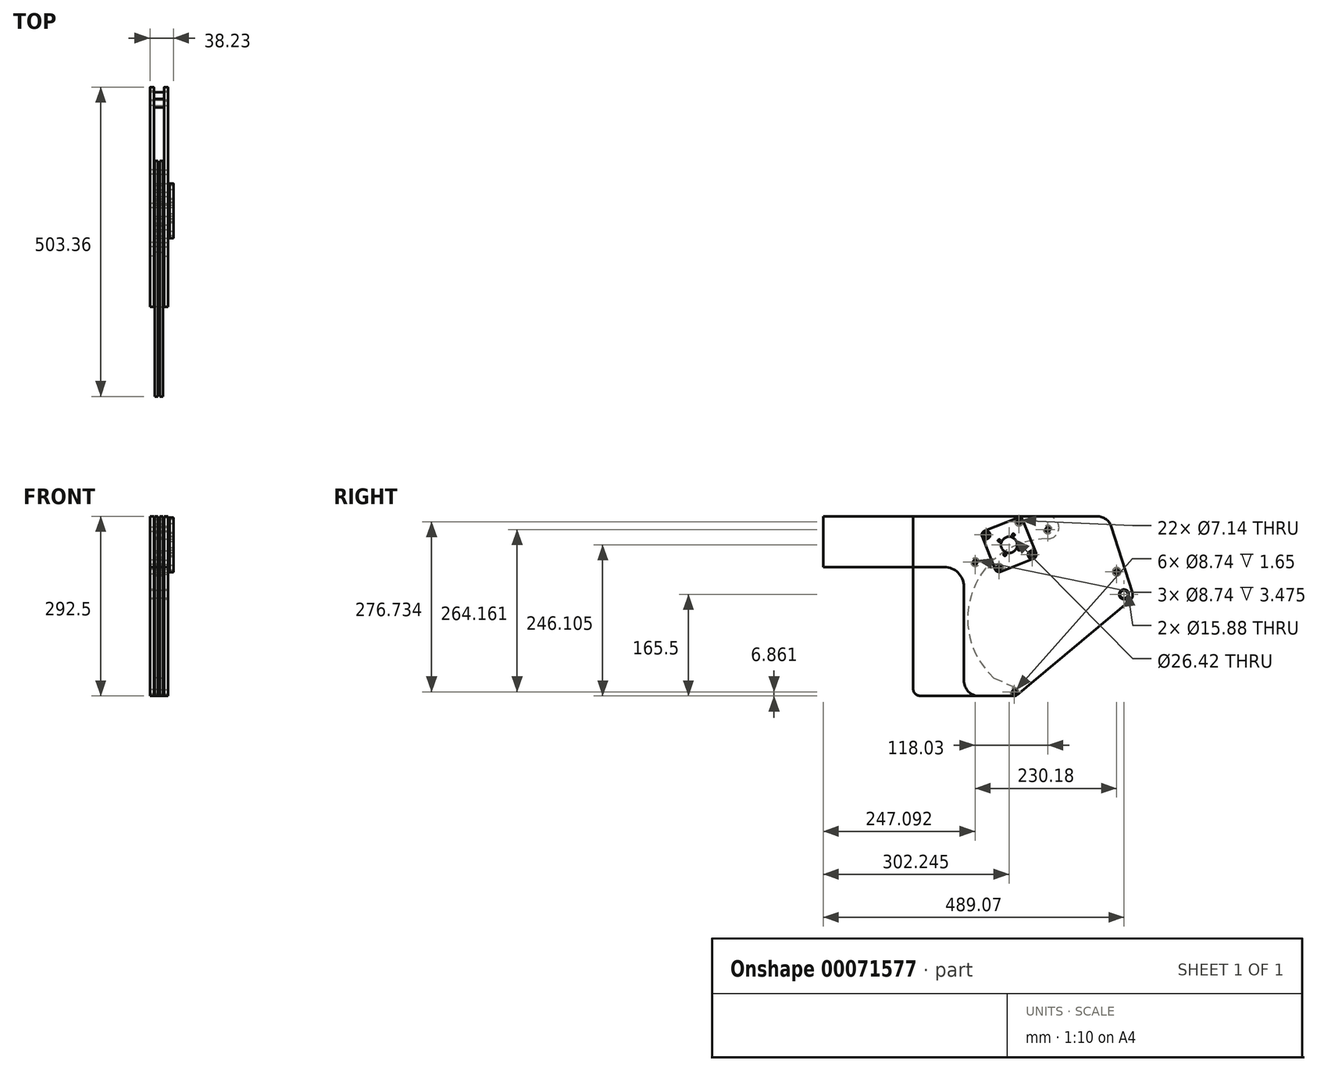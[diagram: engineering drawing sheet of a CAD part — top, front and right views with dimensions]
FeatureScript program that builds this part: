
annotation { "Feature Type Name" : "Feature", "Feature Type Description" : "" }
export const myFeature = defineFeature(function(context is Context, id is Id, definition is map)
    precondition{}
    {
        {
            assignVariable(context, id + "F0", {"name" : "overallWidth", "anyValue" : 29});
        }
        {
            assignVariable(context, id + "F1", {"name" : "bumperGapWidth", "anyValue" : 13});
        }
        {
            var Q0;
            Q0=qCreatedBy(makeId("Right.planeOp"),FACE);
            var sketch = newSketch(context, id + "F2", { "sketchPlane" : qUnion([Q0])});
            skLineSegment(sketch, "E0", {"start": v(0, 0) * mm, "end": v(-374.65, 0) * mm, "construction": true});
            skLineSegment(sketch, "E1", {"start": v(0, 0) * mm, "end": v(0, 234.95) * mm, "construction": true});
            skCircle(sketch, "E2", {"center": v(0, 234.95) * mm, "radius": 6.35 * mm});
            skCircle(sketch, "E3", {"center": v(-178.27, 76.31) * mm, "radius": 3.57 * mm});
            skCircle(sketch, "E4", {"center": v(-67.8, 123.83) * mm, "radius": 123.83 * mm, "construction": true});
            skLineSegment(sketch, "E5.bottom", {"start": v(-343.02, 279.4) * mm, "end": v(-323.97, 279.4) * mm, "construction": true});
            skLineSegment(sketch, "E5.top", {"start": v(-343.02, 152.4) * mm, "end": v(-323.97, 152.4) * mm, "construction": true});
            skLineSegment(sketch, "E5.left", {"start": v(-343.02, 279.4) * mm, "end": v(-343.02, 152.4) * mm, "construction": true});
            skLineSegment(sketch, "E5.right", {"start": v(-323.97, 279.4) * mm, "end": v(-323.97, 152.4) * mm, "construction": true});
            skCircle(sketch, "E6", {"center": v(-292.22, 184.15) * mm, "radius": 31.75 * mm, "construction": true});
            skCircle(sketch, "E7", {"center": v(-292.22, 247.65) * mm, "radius": 31.75 * mm, "construction": true});
            skLineSegment(sketch, "E8", {"start": v(-323.97, 279.4) * mm, "end": v(-292.22, 279.4) * mm, "construction": true});
            skLineSegment(sketch, "E9", {"start": v(-260.47, 247.65) * mm, "end": v(-260.47, 184.15) * mm, "construction": true});
            skLineSegment(sketch, "E10", {"start": v(-323.97, 152.4) * mm, "end": v(-292.22, 152.4) * mm, "construction": true});
            skCircle(sketch, "E11", {"center": v(-123.95, 195.17) * mm, "radius": 123.83 * mm, "construction": true});
            skLineSegment(sketch, "E12", {"start": v(-343.02, 361.95) * mm, "end": v(6.35, 361.95) * mm, "construction": true});
            skLineSegment(sketch, "E13", {"start": v(6.35, 361.95) * mm, "end": v(6.35, 234.95) * mm, "construction": true});
            skCircle(sketch, "E14", {"center": v(-11.8, 271.71) * mm, "radius": 3.57 * mm});
            skCircle(sketch, "E15", {"center": v(-241.98, 287.3) * mm, "radius": 3.57 * mm});
            skCircle(sketch, "E16", {"center": v(-123.95, 340.47) * mm, "radius": 3.57 * mm});
            skLineSegment(sketch, "E17", {"start": v(0, 234.95) * mm, "end": v(-11.8, 271.71) * mm, "construction": true});
            skLineSegment(sketch, "E18", {"start": v(-6.05, 233) * mm, "end": v(-17.84, 269.77) * mm, "construction": true});
            skLineSegment(sketch, "E19", {"start": v(-123.95, 319) * mm, "end": v(-123.95, 361.95) * mm, "construction": true});
            skCircle(sketch, "E20", {"center": v(-178.27, 76.31) * mm, "radius": 4.37 * mm});
            skCircle(sketch, "E21", {"center": v(-178.27, 76.31) * mm, "radius": 6.86 * mm});
            skCircle(sketch, "E22", {"center": v(-241.98, 287.3) * mm, "radius": 4.37 * mm});
            skCircle(sketch, "E23", {"center": v(-241.98, 287.3) * mm, "radius": 6.86 * mm});
            skCircle(sketch, "E24", {"center": v(-123.95, 340.47) * mm, "radius": 4.37 * mm});
            skCircle(sketch, "E25", {"center": v(-123.95, 340.47) * mm, "radius": 6.86 * mm});
            skCircle(sketch, "E26", {"center": v(-11.8, 271.71) * mm, "radius": 4.37 * mm});
            skCircle(sketch, "E27", {"center": v(-11.8, 271.71) * mm, "radius": 6.86 * mm});
            skSolve(sketch);
        }
        {
            var Q0;
            Q0=qCreatedBy(makeId("Right.planeOp"),FACE);
            cPlane(context, id + "F3", {"entities" : qUnion([Q0]), "cplaneType" : CPlaneType.OFFSET, "offset" : (getVariable(context, 'bumperGapWidth') / 2) * mm, "width" : 152.4 * mm, "height" : 152.4 * mm});
        }
        {
            var Q0;
            Q0=qCreatedBy(makeId("Right.planeOp"),FACE);
            cPlane(context, id + "F4", {"entities" : qUnion([Q0]), "cplaneType" : CPlaneType.OFFSET, "offset" : (getVariable(context, 'overallWidth') / 2) * mm, "width" : 152.4 * mm, "height" : 152.4 * mm});
        }
        {
            var Q0;
            Q0=qCreatedBy(id+"F4.planeOp",FACE);
            var sketch = newSketch(context, id + "F5", { "sketchPlane" : qUnion([Q0])});
            skCircle(sketch, "E28.0", {"center": v(-178.27, 76.31) * mm, "radius": 6.86 * mm});
            skCircle(sketch, "E28.1", {"center": v(-178.27, 76.31) * mm, "radius": 3.57 * mm});
            skCircle(sketch, "E28.7", {"center": v(-241.98, 287.3) * mm, "radius": 3.57 * mm});
            skCircle(sketch, "E28.8", {"center": v(-123.95, 340.47) * mm, "radius": 3.57 * mm});
            skCircle(sketch, "E28.9", {"center": v(-11.8, 271.71) * mm, "radius": 3.57 * mm});
            skLineSegment(sketch, "E29.0", {"start": v(-343.02, 279.4) * mm, "end": v(-323.97, 279.4) * mm, "construction": true});
            skLineSegment(sketch, "E29.1", {"start": v(-323.97, 279.4) * mm, "end": v(-292.22, 279.4) * mm, "construction": true});
            skCircle(sketch, "E29.2", {"center": v(-292.22, 247.65) * mm, "radius": 31.75 * mm, "construction": true});
            skLineSegment(sketch, "E30", {"start": v(-260.47, 247.65) * mm, "end": v(-260.47, 94.85) * mm});
            skLineSegment(sketch, "E31", {"start": v(-235.07, 69.45) * mm, "end": v(-178.27, 69.45) * mm});
            skArc(sketch, "E32", {"start": v(-260.47, 247.65) * mm, "mid": v(-269.77, 270.1) * mm, "end": v(-292.22, 279.4) * mm});
            skPoint(sketch, "E33.visualSharp", {"position": v(-260.47, 69.45) * mm});
            skArc(sketch, "E33.filletArc", {"start": v(-260.47, 94.85) * mm, "mid": v(-253.03, 76.9) * mm, "end": v(-235.07, 69.45) * mm});
            skCircle(sketch, "E34", {"center": v(0, 234.95) * mm, "radius": 7.94 * mm});
            skCircle(sketch, "E35", {"center": v(0, 234.95) * mm, "radius": 14.29 * mm, "construction": true});
            skLineSegment(sketch, "E36", {"start": v(-173.87, 71.05) * mm, "end": v(9.16, 223.99) * mm});
            skLineSegment(sketch, "E37", {"start": v(13.6, 239.32) * mm, "end": v(-20.1, 344.31) * mm});
            skLineSegment(sketch, "E38.0", {"start": v(-343.02, 361.95) * mm, "end": v(6.35, 361.95) * mm, "construction": true});
            skLineSegment(sketch, "E39", {"start": v(-44.28, 361.95) * mm, "end": v(-343.02, 361.95) * mm});
            skLineSegment(sketch, "E40", {"start": v(-343.02, 361.95) * mm, "end": v(-343.02, 279.4) * mm});
            skArc(sketch, "E41", {"start": v(-178.27, 69.45) * mm, "mid": v(-175.93, 69.86) * mm, "end": v(-173.87, 71.05) * mm});
            skArc(sketch, "E42", {"start": v(9.16, 223.99) * mm, "mid": v(13.72, 230.97) * mm, "end": v(13.6, 239.32) * mm});
            skLineSegment(sketch, "E43", {"start": v(-343.02, 279.4) * mm, "end": v(-292.22, 279.4) * mm, "construction": true});
            skLineSegment(sketch, "E44", {"start": v(-343.02, 279.4) * mm, "end": v(-292.22, 279.4) * mm});
            skPoint(sketch, "E45.visualSharp", {"position": v(-25.75, 361.95) * mm});
            skArc(sketch, "E45.filletArc", {"start": v(-20.1, 344.31) * mm, "mid": v(-29.31, 357.07) * mm, "end": v(-44.28, 361.95) * mm});
            skSolve(sketch);
        }
        {
            var Q0;
            Q0 = qSketchRegion(id + "F5", true);
            extrude(context, id + "F6", {"entities" : qUnion([Q0]), "oppositeDirection" : true, "depth" : 6.35 * mm});
        }
        {
            var Q0;
            Q0=qCreatedBy(id+"F3.planeOp",FACE);
            var sketch = newSketch(context, id + "F7", { "sketchPlane" : qUnion([Q0])});
            skCircle(sketch, "E46.0", {"center": v(-123.95, 195.17) * mm, "radius": 123.83 * mm, "construction": true});
            skCircle(sketch, "E47", {"center": v(-123.95, 195.17) * mm, "radius": 130.18 * mm, "construction": true});
            skLineSegment(sketch, "E48.0", {"start": v(-343.02, 279.4) * mm, "end": v(-323.97, 279.4) * mm, "construction": true});
            skLineSegment(sketch, "E49.0", {"start": v(-323.97, 279.4) * mm, "end": v(-323.97, 152.4) * mm, "construction": true});
            skLineSegment(sketch, "E50", {"start": v(-362.07, 361.95) * mm, "end": v(-362.07, 279.4) * mm, "construction": true});
            skLineSegment(sketch, "E51", {"start": v(-362.07, 279.4) * mm, "end": v(-343.02, 279.4) * mm});
            skLineSegment(sketch, "E52", {"start": v(-343.02, 279.4) * mm, "end": v(-343.02, 152.4) * mm});
            skCircle(sketch, "E53.0", {"center": v(-178.27, 76.31) * mm, "radius": 3.57 * mm, "construction": true});
            skLineSegment(sketch, "E54", {"start": v(-343.02, 82.15) * mm, "end": v(-343.02, 152.4) * mm});
            skArc(sketch, "E55", {"start": v(-211.94, 99.24) * mm, "mid": v(-245.26, 242.38) * mm, "end": v(-123.95, 325.34) * mm});
            skLineSegment(sketch, "E56", {"start": v(-211.94, 99.24) * mm, "end": v(-175.42, 82.55) * mm});
            skCircle(sketch, "E57.0", {"center": v(-178.27, 76.31) * mm, "radius": 6.86 * mm, "construction": true});
            skArc(sketch, "E58", {"start": v(-178.27, 69.45) * mm, "mid": v(-171.57, 74.85) * mm, "end": v(-175.42, 82.55) * mm, "construction": true});
            skLineSegment(sketch, "E59", {"start": v(-178.27, 69.45) * mm, "end": v(-330.32, 69.45) * mm});
            skCircle(sketch, "E60.0", {"center": v(-241.98, 287.3) * mm, "radius": 3.57 * mm});
            skCircle(sketch, "E61.0", {"center": v(-123.95, 340.47) * mm, "radius": 3.57 * mm});
            skArc(sketch, "E62", {"start": v(-178.27, 69.45) * mm, "mid": v(-171.57, 74.85) * mm, "end": v(-175.42, 82.55) * mm});
            skCircle(sketch, "E63.0", {"center": v(-178.27, 76.31) * mm, "radius": 3.57 * mm});
            skPoint(sketch, "E64.visualSharp", {"position": v(-343.02, 69.45) * mm});
            skArc(sketch, "E64.filletArc", {"start": v(-343.02, 82.15) * mm, "mid": v(-339.3, 73.17) * mm, "end": v(-330.32, 69.45) * mm});
            skArc(sketch, "E65", {"start": v(-123.95, 325.34) * mm, "mid": v(-105.65, 343.65) * mm, "end": v(-123.95, 361.95) * mm});
            skLineSegment(sketch, "E66", {"start": v(-123.95, 361.95) * mm, "end": v(-362.07, 361.95) * mm});
            skLineSegment(sketch, "E67", {"start": v(-362.07, 361.95) * mm, "end": v(-489.07, 361.95) * mm});
            skLineSegment(sketch, "E68", {"start": v(-489.07, 361.95) * mm, "end": v(-489.07, 279.4) * mm});
            skLineSegment(sketch, "E69", {"start": v(-489.07, 279.4) * mm, "end": v(-362.07, 279.4) * mm});
            skSolve(sketch);
        }
        {
            var Q0;
            Q0 = qSketchRegion(id + "F7", true);
            extrude(context, id + "F8", {"entities" : qUnion([Q0]), "oppositeDirection" : true, "depth" : 4.76 * mm});
        }
        {
            var Q0;
            Q0=makeQuery(id+"F8.opExtrude","CAP_FACE",FACE,{"disambiguationData":[OSD([sQuery(id+"F7.wireOp",EDGE,"FGU2iulP-mEND-ptDn-2N6M-zOusOUoRXGuS"),sQuery(id+"F7.wireOp",EDGE,"dHuU5Xxs-PWdM-lHFD-YR0q-5kX4qnVROPGa"),sQuery(id+"F7.wireOp",EDGE,"emKYSds7-kRQy-B5Ny-Edj4-jaAremwDHOBO"),sQuery(id+"F7.wireOp",EDGE,"E50"),sQuery(id+"F7.wireOp",EDGE,"E51"),sQuery(id+"F7.wireOp",EDGE,"E52"),sQuery(id+"F7.wireOp",EDGE,"E54"),sQuery(id+"F7.wireOp",EDGE,"E55"),sQuery(id+"F7.wireOp",EDGE,"a4eece87-18dd-42ed-a909-83406d0543b2"),sQuery(id+"F7.wireOp",EDGE,"E56"),sQuery(id+"F7.wireOp",EDGE,"E59"),sQuery(id+"F7.wireOp",EDGE,"E60.0"),sQuery(id+"F7.wireOp",EDGE,"E61.0"),sQuery(id+"F7.wireOp",EDGE,"e2687a6c-33c6-4455-bcdd-d88ace95f83b.0"),sQuery(id+"F7.wireOp",EDGE,"E62"),sQuery(id+"F7.wireOp",EDGE,"E63.0"),sQuery(id+"F7.wireOp",EDGE,"eee57473-292c-4d81-84d7-392532a5bbb9.filletArc"),sQuery(id+"F7.wireOp",EDGE,"E64.filletArc")])],"isStart":true});
            var sketch = newSketch(context, id + "F9", { "sketchPlane" : qUnion([Q0])});
            skCircle(sketch, "E70.0", {"center": v(-241.98, 287.3) * mm, "radius": 6.86 * mm});
            skCircle(sketch, "E70.1", {"center": v(-241.98, 287.3) * mm, "radius": 4.37 * mm});
            skCircle(sketch, "E70.2", {"center": v(-123.95, 340.47) * mm, "radius": 6.86 * mm});
            skCircle(sketch, "E70.3", {"center": v(-123.95, 340.47) * mm, "radius": 4.37 * mm});
            skCircle(sketch, "E70.4", {"center": v(-11.8, 271.71) * mm, "radius": 6.86 * mm});
            skCircle(sketch, "E70.5", {"center": v(-11.8, 271.71) * mm, "radius": 4.37 * mm});
            skCircle(sketch, "E70.6", {"center": v(-178.27, 76.31) * mm, "radius": 6.86 * mm});
            skCircle(sketch, "E70.7", {"center": v(-178.27, 76.31) * mm, "radius": 4.37 * mm});
            skSolve(sketch);
        }
        {
            var Q0;
            Q0=makeQuery(id+"F9.imprint","IMPRINT",FACE,{"disambiguationData":[TD([[makeQuery(id+"F9.imprint","IMPRINT",EDGE,{"derivedFrom":sQuery(id+"F9.wireOp",EDGE,"E70.2")}),1.0]])]});
            var Q1;
            Q1=makeQuery(id+"F9.imprint","IMPRINT",FACE,{"disambiguationData":[TD([[makeQuery(id+"F9.imprint","IMPRINT",EDGE,{"derivedFrom":sQuery(id+"F9.wireOp",EDGE,"E70.0")}),1.0]])]});
            var Q2;
            Q2=makeQuery(id+"F9.imprint","IMPRINT",FACE,{"disambiguationData":[TD([[makeQuery(id+"F9.imprint","IMPRINT",EDGE,{"derivedFrom":sQuery(id+"F9.wireOp",EDGE,"E70.7")}),-1.0]])]});
            var Q3;
            Q3=makeQuery(id+"F6.opExtrude","CAP_FACE",FACE,{"disambiguationData":[OSD([sQuery(id+"F5.wireOp",EDGE,"E28.0"),sQuery(id+"F5.wireOp",EDGE,"E28.1"),sQuery(id+"F5.wireOp",EDGE,"E28.2"),sQuery(id+"F5.wireOp",EDGE,"E28.3"),sQuery(id+"F5.wireOp",EDGE,"E28.4"),sQuery(id+"F5.wireOp",EDGE,"E28.5"),sQuery(id+"F5.wireOp",EDGE,"E28.6"),sQuery(id+"F5.wireOp",EDGE,"E28.7"),sQuery(id+"F5.wireOp",EDGE,"E28.8"),sQuery(id+"F5.wireOp",EDGE,"E28.9"),sQuery(id+"F5.wireOp",EDGE,"0DRxkcYK-P67Z-hc5T-PIY5-J2nq71u3PR2t"),sQuery(id+"F5.wireOp",EDGE,"E30"),sQuery(id+"F5.wireOp",EDGE,"E31"),sQuery(id+"F5.wireOp",EDGE,"xV87OUrw-cdUr-jH3c-AOfr-qMSfTrLvHBVd"),sQuery(id+"F5.wireOp",EDGE,"E32"),sQuery(id+"F5.wireOp",EDGE,"E33.filletArc")])],"isStart":false});
            extrude(context, id + "F10", {"entities" : qUnion([Q0, Q1, Q2]), "endBound" : BoundingType.UP_TO_SURFACE, "endBoundEntityFace" : qUnion([Q3]), "depth" : 25.4 * mm});
        }
        {
            var Q0;
            Q0=makeQuery(id+"F8.opExtrude","SWEPT_BODY",BODY,{"disambiguationData":[OSD([sQuery(id+"F7.wireOp",EDGE,"FGU2iulP-mEND-ptDn-2N6M-zOusOUoRXGuS"),sQuery(id+"F7.wireOp",EDGE,"dHuU5Xxs-PWdM-lHFD-YR0q-5kX4qnVROPGa"),sQuery(id+"F7.wireOp",EDGE,"emKYSds7-kRQy-B5Ny-Edj4-jaAremwDHOBO"),sQuery(id+"F7.wireOp",EDGE,"E50"),sQuery(id+"F7.wireOp",EDGE,"E51"),sQuery(id+"F7.wireOp",EDGE,"E52"),sQuery(id+"F7.wireOp",EDGE,"E54"),sQuery(id+"F7.wireOp",EDGE,"E55"),sQuery(id+"F7.wireOp",EDGE,"a4eece87-18dd-42ed-a909-83406d0543b2"),sQuery(id+"F7.wireOp",EDGE,"E56"),sQuery(id+"F7.wireOp",EDGE,"E59"),sQuery(id+"F7.wireOp",EDGE,"E60.0"),sQuery(id+"F7.wireOp",EDGE,"E61.0"),sQuery(id+"F7.wireOp",EDGE,"e2687a6c-33c6-4455-bcdd-d88ace95f83b.0"),sQuery(id+"F7.wireOp",EDGE,"E62"),sQuery(id+"F7.wireOp",EDGE,"E63.0"),sQuery(id+"F7.wireOp",EDGE,"eee57473-292c-4d81-84d7-392532a5bbb9.filletArc"),sQuery(id+"F7.wireOp",EDGE,"E64.filletArc")])]});
            var Q1;
            Q1=makeQuery(id+"F6.opExtrude","SWEPT_BODY",BODY,{"disambiguationData":[OSD([sQuery(id+"F5.wireOp",EDGE,"E28.0"),sQuery(id+"F5.wireOp",EDGE,"E28.1"),sQuery(id+"F5.wireOp",EDGE,"E28.2"),sQuery(id+"F5.wireOp",EDGE,"E28.3"),sQuery(id+"F5.wireOp",EDGE,"E28.4"),sQuery(id+"F5.wireOp",EDGE,"E28.5"),sQuery(id+"F5.wireOp",EDGE,"E28.6"),sQuery(id+"F5.wireOp",EDGE,"E28.7"),sQuery(id+"F5.wireOp",EDGE,"E28.8"),sQuery(id+"F5.wireOp",EDGE,"E28.9"),sQuery(id+"F5.wireOp",EDGE,"0DRxkcYK-P67Z-hc5T-PIY5-J2nq71u3PR2t"),sQuery(id+"F5.wireOp",EDGE,"E30"),sQuery(id+"F5.wireOp",EDGE,"E31"),sQuery(id+"F5.wireOp",EDGE,"xV87OUrw-cdUr-jH3c-AOfr-qMSfTrLvHBVd"),sQuery(id+"F5.wireOp",EDGE,"E32"),sQuery(id+"F5.wireOp",EDGE,"E33.filletArc")])]});
            var Q2;
            Q2=makeQuery(id+"F10.opExtrude","SWEPT_BODY",BODY,{"disambiguationData":[OSD([sQuery(id+"F9.wireOp",EDGE,"E70.2"),sQuery(id+"F9.wireOp",EDGE,"E70.3")])]});
            var Q3;
            Q3=makeQuery(id+"F10.opExtrude","SWEPT_BODY",BODY,{"disambiguationData":[OSD([sQuery(id+"F9.wireOp",EDGE,"E70.4"),sQuery(id+"F9.wireOp",EDGE,"E70.5")])]});
            var Q4;
            Q4=makeQuery(id+"F10.opExtrude","SWEPT_BODY",BODY,{"disambiguationData":[OSD([sQuery(id+"F9.wireOp",EDGE,"E70.6"),sQuery(id+"F9.wireOp",EDGE,"E70.7")])]});
            var Q5;
            Q5=makeQuery(id+"F10.opExtrude","SWEPT_BODY",BODY,{"disambiguationData":[OSD([sQuery(id+"F9.wireOp",EDGE,"E70.0"),sQuery(id+"F9.wireOp",EDGE,"E70.1")])]});
            var Q6;
            Q6=qCreatedBy(makeId("Right.planeOp"),FACE);
            mirror(context, id + "F11", {"entities" : qUnion([Q0, Q1, Q2, Q3, Q4, Q5]), "mirrorPlane" : qUnion([Q6])});
        }
        {
            var Q0;
            Q0=makeQuery(id+"F9.imprint","IMPRINT",FACE,{"disambiguationData":[TD([[makeQuery(id+"F9.imprint","IMPRINT",EDGE,{"derivedFrom":sQuery(id+"F9.wireOp",EDGE,"E70.4")}),1.0]])]});
            extrude(context, id + "F12", {"entities" : qUnion([Q0]), "endBound" : BoundingType.UP_TO_NEXT, "depth" : 25.4 * mm, "hasSecondDirection" : true, "secondDirectionBound" : SecondDirectionBoundingType.UP_TO_NEXT, "secondDirectionOppositeDirection" : true, "secondDirectionDepth" : 25.4 * mm});
        }
        {
            var Q0;
            Q0=makeQuery(id+"F11.opPattern","COPY",FACE,{"derivedFrom":makeQuery(id+"F8.opExtrude","CAP_FACE",FACE,{"disambiguationData":[OSD([sQuery(id+"F7.wireOp",EDGE,"FGU2iulP-mEND-ptDn-2N6M-zOusOUoRXGuS"),sQuery(id+"F7.wireOp",EDGE,"dHuU5Xxs-PWdM-lHFD-YR0q-5kX4qnVROPGa"),sQuery(id+"F7.wireOp",EDGE,"emKYSds7-kRQy-B5Ny-Edj4-jaAremwDHOBO"),sQuery(id+"F7.wireOp",EDGE,"E50"),sQuery(id+"F7.wireOp",EDGE,"E51"),sQuery(id+"F7.wireOp",EDGE,"E52"),sQuery(id+"F7.wireOp",EDGE,"E54"),sQuery(id+"F7.wireOp",EDGE,"E55"),sQuery(id+"F7.wireOp",EDGE,"a4eece87-18dd-42ed-a909-83406d0543b2"),sQuery(id+"F7.wireOp",EDGE,"E56"),sQuery(id+"F7.wireOp",EDGE,"E59"),sQuery(id+"F7.wireOp",EDGE,"E60.0"),sQuery(id+"F7.wireOp",EDGE,"E61.0"),sQuery(id+"F7.wireOp",EDGE,"e2687a6c-33c6-4455-bcdd-d88ace95f83b.0"),sQuery(id+"F7.wireOp",EDGE,"E62"),sQuery(id+"F7.wireOp",EDGE,"E63.0"),sQuery(id+"F7.wireOp",EDGE,"eee57473-292c-4d81-84d7-392532a5bbb9.filletArc"),sQuery(id+"F7.wireOp",EDGE,"E64.filletArc")])],"isStart":false}),"instanceName":"1"});
            var sketch = newSketch(context, id + "F13", { "sketchPlane" : qUnion([Q0])});
            skCircle(sketch, "E71.0", {"center": v(-241.98, 287.3) * mm, "radius": 4.37 * mm});
            skCircle(sketch, "E71.1", {"center": v(-241.98, 287.3) * mm, "radius": 6.86 * mm});
            skCircle(sketch, "E71.2", {"center": v(-123.95, 340.47) * mm, "radius": 6.86 * mm});
            skCircle(sketch, "E71.3", {"center": v(-123.95, 340.47) * mm, "radius": 4.37 * mm});
            skCircle(sketch, "E71.6", {"center": v(-178.27, 76.31) * mm, "radius": 6.86 * mm});
            skCircle(sketch, "E71.7", {"center": v(-178.27, 76.31) * mm, "radius": 4.37 * mm});
            skSolve(sketch);
        }
        {
            var Q0;
            Q0 = qSketchRegion(id + "F13", true);
            var Q1;
            Q1=makeQuery(id+"F8.opExtrude","CAP_FACE",FACE,{"disambiguationData":[OSD([sQuery(id+"F7.wireOp",EDGE,"FGU2iulP-mEND-ptDn-2N6M-zOusOUoRXGuS"),sQuery(id+"F7.wireOp",EDGE,"dHuU5Xxs-PWdM-lHFD-YR0q-5kX4qnVROPGa"),sQuery(id+"F7.wireOp",EDGE,"emKYSds7-kRQy-B5Ny-Edj4-jaAremwDHOBO"),sQuery(id+"F7.wireOp",EDGE,"E50"),sQuery(id+"F7.wireOp",EDGE,"E51"),sQuery(id+"F7.wireOp",EDGE,"E52"),sQuery(id+"F7.wireOp",EDGE,"E54"),sQuery(id+"F7.wireOp",EDGE,"E55"),sQuery(id+"F7.wireOp",EDGE,"a4eece87-18dd-42ed-a909-83406d0543b2"),sQuery(id+"F7.wireOp",EDGE,"E56"),sQuery(id+"F7.wireOp",EDGE,"E59"),sQuery(id+"F7.wireOp",EDGE,"E60.0"),sQuery(id+"F7.wireOp",EDGE,"E61.0"),sQuery(id+"F7.wireOp",EDGE,"e2687a6c-33c6-4455-bcdd-d88ace95f83b.0"),sQuery(id+"F7.wireOp",EDGE,"E62"),sQuery(id+"F7.wireOp",EDGE,"E63.0"),sQuery(id+"F7.wireOp",EDGE,"eee57473-292c-4d81-84d7-392532a5bbb9.filletArc"),sQuery(id+"F7.wireOp",EDGE,"E64.filletArc")])],"isStart":false});
            extrude(context, id + "F14", {"entities" : qUnion([Q0]), "endBound" : BoundingType.UP_TO_SURFACE, "endBoundEntityFace" : qUnion([Q1]), "depth" : 25.4 * mm});
        }
        {
            var Q0;
            Q0=makeQuery(id+"F2.imprint","IMPRINT",FACE,{"disambiguationData":[TD([[makeQuery(id+"F2.imprint","IMPRINT",EDGE,{"derivedFrom":sQuery(id+"F2.wireOp",EDGE,"E2")}),1.0]])]});
            var Q1;
            Q1=sQuery(id+"F2.wireOp",EDGE,"E2");
            extrude(context, id + "F15", {"entities" : qUnion([Q0]), "surfaceEntities" : qUnion([Q1]), "depth" : (getVariable(context, 'overallWidth') / 2 + 1 / 8) * mm, "hasSecondDirection" : true, "secondDirectionOppositeDirection" : true, "secondDirectionDepth" : (getVariable(context, 'overallWidth') / 2 + 1 / 8) * mm});
        }
        {
            var Q0;
            Q0=makeQuery(id+"F11.opPattern","COPY",FACE,{"derivedFrom":makeQuery(id+"F6.opExtrude","CAP_FACE",FACE,{"disambiguationData":[OSD([sQuery(id+"F5.wireOp",EDGE,"E28.1"),sQuery(id+"F5.wireOp",EDGE,"E28.7"),sQuery(id+"F5.wireOp",EDGE,"E28.8"),sQuery(id+"F5.wireOp",EDGE,"E28.9"),sQuery(id+"F5.wireOp",EDGE,"E30"),sQuery(id+"F5.wireOp",EDGE,"E31"),sQuery(id+"F5.wireOp",EDGE,"E32"),sQuery(id+"F5.wireOp",EDGE,"E33.filletArc"),sQuery(id+"F5.wireOp",EDGE,"E34"),sQuery(id+"F5.wireOp",EDGE,"E36"),sQuery(id+"F5.wireOp",EDGE,"E37"),sQuery(id+"F5.wireOp",EDGE,"E39"),sQuery(id+"F5.wireOp",EDGE,"E40"),sQuery(id+"F5.wireOp",EDGE,"E28.0"),sQuery(id+"F5.wireOp",EDGE,"E42"),sQuery(id+"F5.wireOp",EDGE,"E44"),sQuery(id+"F5.wireOp",EDGE,"E45.filletArc")])],"isStart":false}),"instanceName":"1"});
            var sketch = newSketch(context, id + "F16", { "sketchPlane" : qUnion([Q0])});
            skCircle(sketch, "E72.0", {"center": v(0, 234.95) * mm, "radius": 6.35 * mm, "construction": true});
            skCircle(sketch, "E73", {"center": v(0, 234.95) * mm, "radius": 14.68 * mm});
            skCircle(sketch, "E74", {"center": v(0, 234.95) * mm, "radius": 17.86 * mm});
            skSolve(sketch);
        }
        {
            var Q0;
            Q0=makeQuery(id+"F16.imprint","IMPRINT",FACE,{"disambiguationData":[TD([[makeQuery(id+"F16.imprint","IMPRINT",EDGE,{"derivedFrom":makeQuery(id+"F11.opPattern","COPY",EDGE,{"derivedFrom":makeQuery(id+"F6.opExtrude","CAP_EDGE",EDGE,{"disambiguationData":[OSD([sQuery(id+"F5.wireOp",EDGE,"E28.1")])],"isStart":false}),"instanceName":"1"})}),-1.0]])]});
            cPlane(context, id + "F17", {"entities" : qUnion([Q0]), "cplaneType" : CPlaneType.OFFSET, "offset" : 25.4 * mm, "width" : 152.4 * mm, "height" : 152.4 * mm});
        }
        {
            var Q0;
            Q0=qCreatedBy(id+"F17.planeOp",FACE);
            var sketch = newSketch(context, id + "F18", { "sketchPlane" : qUnion([Q0])});
            skLineSegment(sketch, "E75.bottom", {"start": v(-226.85, 338.1) * mm, "end": v(-173.18, 359.42) * mm});
            skLineSegment(sketch, "E75.top", {"start": v(-200.47, 271.7) * mm, "end": v(-146.8, 293) * mm});
            skLineSegment(sketch, "E75.left", {"start": v(-230.69, 329.2) * mm, "end": v(-209.37, 275.53) * mm});
            skLineSegment(sketch, "E75.right", {"start": v(-164.28, 355.58) * mm, "end": v(-142.96, 301.91) * mm});
            skLineSegment(sketch, "E76", {"start": v(-233.22, 335.57) * mm, "end": v(0, 234.95) * mm, "construction": true});
            skCircle(sketch, "E77.0", {"center": v(0, 234.95) * mm, "radius": 6.35 * mm});
            skLineSegment(sketch, "E78.0", {"start": v(-343.02, 361.95) * mm, "end": v(6.35, 361.95) * mm, "construction": true});
            skPoint(sketch, "E79", {"position": v(-168.34, 361.95) * mm});
            skCircle(sketch, "E80", {"center": v(-170.65, 353.04) * mm, "radius": 6.86 * mm});
            skCircle(sketch, "E81", {"center": v(-224.32, 331.73) * mm, "radius": 6.86 * mm});
            skCircle(sketch, "E82", {"center": v(-149.34, 299.38) * mm, "radius": 6.86 * mm});
            skCircle(sketch, "E83", {"center": v(-203, 278.06) * mm, "radius": 6.86 * mm});
            skCircle(sketch, "E84.0", {"center": v(-241.98, 287.3) * mm, "radius": 6.86 * mm, "construction": true});
            skCircle(sketch, "E85.0", {"center": v(-123.95, 340.47) * mm, "radius": 6.86 * mm, "construction": true});
            skLineSegment(sketch, "E86", {"start": v(-123.95, 340.47) * mm, "end": v(-241.98, 287.3) * mm, "construction": true});
            skPoint(sketch, "E87", {"position": v(-182.96, 313.89) * mm});
            skPoint(sketch, "E88.visualSharp", {"position": v(-166.8, 361.95) * mm});
            skArc(sketch, "E88.filletArc", {"start": v(-164.28, 355.58) * mm, "mid": v(-167.93, 359.34) * mm, "end": v(-173.18, 359.42) * mm});
            skPoint(sketch, "E89.visualSharp", {"position": v(-233.22, 335.57) * mm});
            skArc(sketch, "E89.filletArc", {"start": v(-226.85, 338.1) * mm, "mid": v(-230.61, 334.45) * mm, "end": v(-230.69, 329.2) * mm});
            skPoint(sketch, "E90.visualSharp", {"position": v(-140.43, 295.54) * mm});
            skArc(sketch, "E90.filletArc", {"start": v(-146.8, 293) * mm, "mid": v(-143.04, 296.66) * mm, "end": v(-142.96, 301.91) * mm});
            skPoint(sketch, "E91.visualSharp", {"position": v(-206.84, 269.16) * mm});
            skArc(sketch, "E91.filletArc", {"start": v(-209.37, 275.53) * mm, "mid": v(-205.72, 271.77) * mm, "end": v(-200.47, 271.7) * mm});
            skLineSegment(sketch, "E92", {"start": v(-203, 278.06) * mm, "end": v(-170.65, 353.04) * mm, "construction": true});
            skCircle(sketch, "E93", {"center": v(-186.83, 315.55) * mm, "radius": 13.2 * mm});
            skCircle(sketch, "E94", {"center": v(-186.83, 315.55) * mm, "radius": 17.5 * mm, "construction": true});
            skCircle(sketch, "E95", {"center": v(-202.9, 322.49) * mm, "radius": 1.98 * mm});
            skCircle(sketch, "E96", {"center": v(-179.9, 331.62) * mm, "radius": 1.98 * mm});
            skCircle(sketch, "E97", {"center": v(-170.76, 308.62) * mm, "radius": 1.98 * mm});
            skCircle(sketch, "E98", {"center": v(-193.76, 299.49) * mm, "radius": 1.98 * mm});
            skCircle(sketch, "E99", {"center": v(-224.32, 331.73) * mm, "radius": 3.57 * mm});
            skCircle(sketch, "E100", {"center": v(-170.65, 353.04) * mm, "radius": 3.57 * mm});
            skCircle(sketch, "E101", {"center": v(-149.34, 299.38) * mm, "radius": 3.57 * mm});
            skCircle(sketch, "E102", {"center": v(-203, 278.06) * mm, "radius": 3.57 * mm});
            skSolve(sketch);
        }
        {
            var Q0;
            Q0=makeQuery(id+"F18.imprint","IMPRINT",FACE,{"disambiguationData":[TD([[makeQuery(id+"F18.imprint","IMPRINT",EDGE,{"derivedFrom":sQuery(id+"F18.wireOp",EDGE,"E75.bottom")}),-1.0]])]});
            var Q1;
            Q1=makeQuery(id+"F18.imprint","IMPRINT",FACE,{"disambiguationData":[TD([[makeQuery(id+"F18.imprint","IMPRINT",EDGE,{"derivedFrom":sQuery(id+"F18.wireOp",EDGE,"E100")}),-1.0]])]});
            var Q2;
            Q2=makeQuery(id+"F18.imprint","IMPRINT",FACE,{"disambiguationData":[TD([[makeQuery(id+"F18.imprint","IMPRINT",EDGE,{"derivedFrom":sQuery(id+"F18.wireOp",EDGE,"E99")}),-1.0]])]});
            var Q3;
            Q3=makeQuery(id+"F18.imprint","IMPRINT",FACE,{"disambiguationData":[TD([[makeQuery(id+"F18.imprint","IMPRINT",EDGE,{"derivedFrom":sQuery(id+"F18.wireOp",EDGE,"E101")}),-1.0]])]});
            var Q4;
            Q4=makeQuery(id+"F18.imprint","IMPRINT",FACE,{"disambiguationData":[TD([[makeQuery(id+"F18.imprint","IMPRINT",EDGE,{"derivedFrom":sQuery(id+"F18.wireOp",EDGE,"E102")}),-1.0]])]});
            extrude(context, id + "F19", {"entities" : qUnion([Q0, Q1, Q2, Q3, Q4]), "depth" : 6.35 * mm});
        }
        {
            var Q0;
            Q0=makeQuery(id+"F18.imprint","IMPRINT",FACE,{"disambiguationData":[TD([[makeQuery(id+"F18.imprint","IMPRINT",EDGE,{"derivedFrom":sQuery(id+"F18.wireOp",EDGE,"E100")}),-1.0]])]});
            var Q1;
            Q1=makeQuery(id+"F18.imprint","IMPRINT",FACE,{"disambiguationData":[TD([[makeQuery(id+"F18.imprint","IMPRINT",EDGE,{"derivedFrom":sQuery(id+"F18.wireOp",EDGE,"E99")}),-1.0]])]});
            var Q2;
            Q2=makeQuery(id+"F18.imprint","IMPRINT",FACE,{"disambiguationData":[TD([[makeQuery(id+"F18.imprint","IMPRINT",EDGE,{"derivedFrom":sQuery(id+"F18.wireOp",EDGE,"E101")}),-1.0]])]});
            var Q3;
            Q3=makeQuery(id+"F18.imprint","IMPRINT",FACE,{"disambiguationData":[TD([[makeQuery(id+"F18.imprint","IMPRINT",EDGE,{"derivedFrom":sQuery(id+"F18.wireOp",EDGE,"E102")}),-1.0]])]});
            var Q4;
            Q4=makeQuery(id+"F11.opPattern","COPY",FACE,{"derivedFrom":makeQuery(id+"F6.opExtrude","CAP_FACE",FACE,{"disambiguationData":[OSD([sQuery(id+"F5.wireOp",EDGE,"E28.1"),sQuery(id+"F5.wireOp",EDGE,"E28.7"),sQuery(id+"F5.wireOp",EDGE,"E28.8"),sQuery(id+"F5.wireOp",EDGE,"E28.9"),sQuery(id+"F5.wireOp",EDGE,"E30"),sQuery(id+"F5.wireOp",EDGE,"E31"),sQuery(id+"F5.wireOp",EDGE,"E32"),sQuery(id+"F5.wireOp",EDGE,"E33.filletArc"),sQuery(id+"F5.wireOp",EDGE,"E34"),sQuery(id+"F5.wireOp",EDGE,"E36"),sQuery(id+"F5.wireOp",EDGE,"E37"),sQuery(id+"F5.wireOp",EDGE,"E39"),sQuery(id+"F5.wireOp",EDGE,"E40"),sQuery(id+"F5.wireOp",EDGE,"E28.0"),sQuery(id+"F5.wireOp",EDGE,"E42"),sQuery(id+"F5.wireOp",EDGE,"E44"),sQuery(id+"F5.wireOp",EDGE,"E45.filletArc")])],"isStart":false}),"instanceName":"1"});
            extrude(context, id + "F20", {"entities" : qUnion([Q0, Q1, Q2, Q3]), "endBound" : BoundingType.UP_TO_SURFACE, "oppositeDirection" : true, "endBoundEntityFace" : qUnion([Q4]), "depth" : 25.4 * mm});
        }
    });
